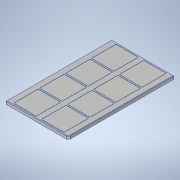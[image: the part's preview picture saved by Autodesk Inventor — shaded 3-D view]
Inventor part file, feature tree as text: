
AUTODESK INVENTOR PART (.ipt)
format: ipt  version: 2022 (Build 260153000, 153)  size: 228,352 bytes
history: native  units: in
note: dims shown in document units (in); Inventor stores cm internally (conversion verified against a paired STEP export)
features: chamfer x3, extrude x2, sketch x2
ambient origin geometry x8: Origin, YZ Plane, XZ Plane, XY Plane, X Axis, Y Axis, Z Axis, Center Point
bodies: Solid1 (feature_tree)
feature tree (7):
  extrude  "Extrusion1"  Depth=8.5in
  extrude  "Extrusion7"  Depth=1.811in
  chamfer  "Chamfer1"  Distance=1.9685in
  chamfer  "Chamfer2"  Distance=0.1378in
  chamfer  "Chamfer3"  Distance=0.4724in
  sketch  "Sketch1"  dims[d0=5.0in d1=8.5in]
  sketch  "Sketch8"  dims[d2=0.25in d3=0.0in d92=1.811in d93=1.9685in d102=0.1378in d104=0.4724in d106=0.0394in d107=1.5748in d109=2.0866in d110=0.7874in d112=2.2441in d115=0.0079in d116=0.0in d117=0.1575in d118=0.0787in d119=45.0deg d120=0.0394in d121=0.0787in d122=45.0deg d123=0.0394in d124=0.0787in d125=45.0deg]
